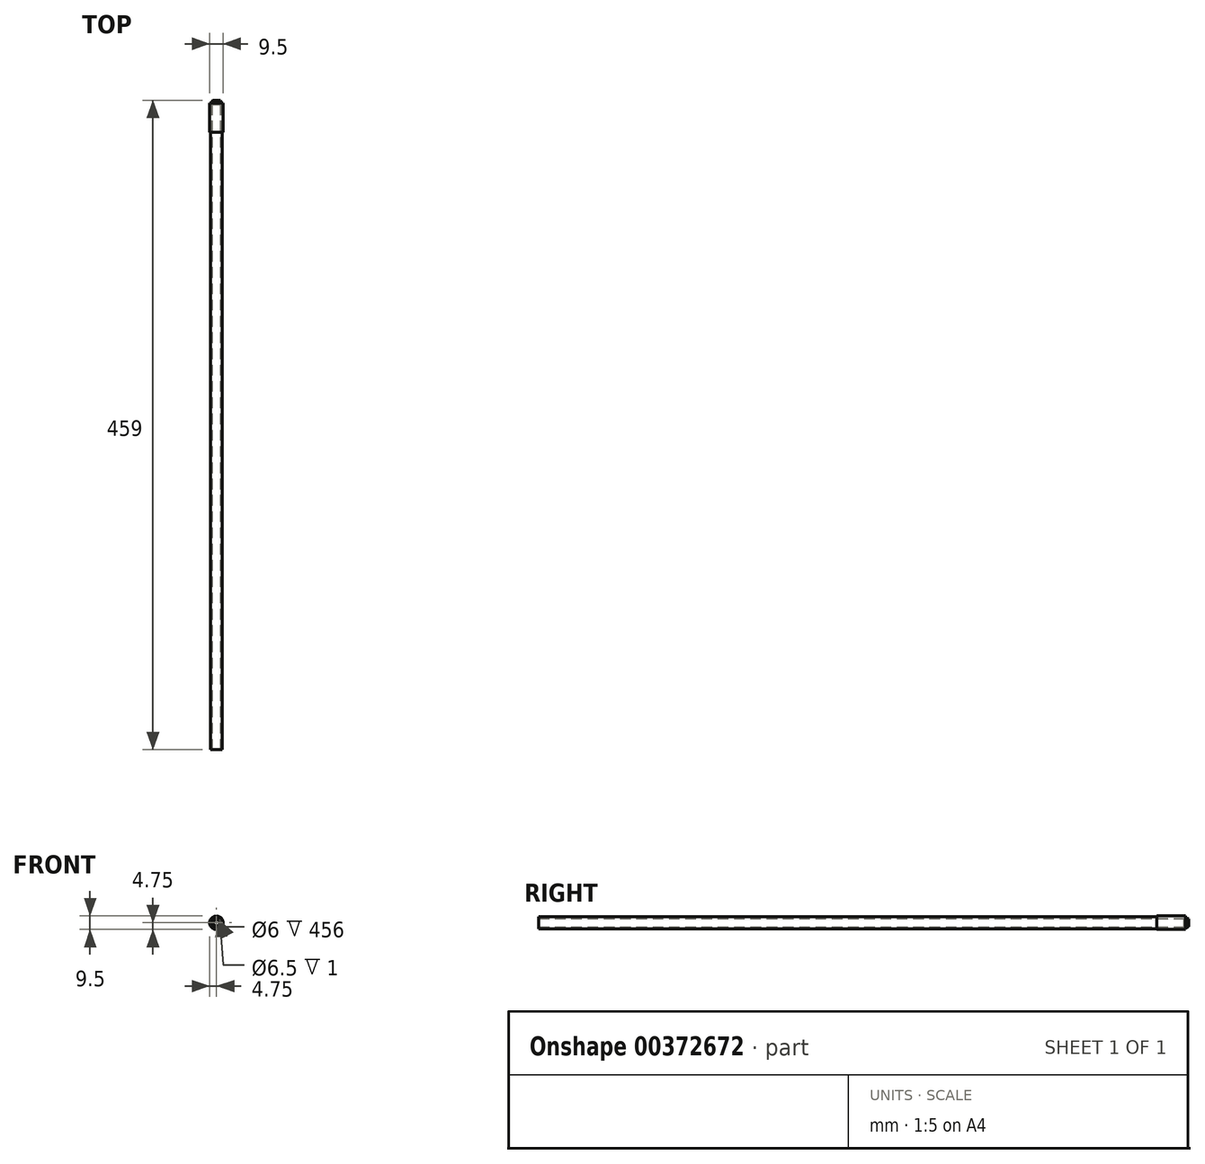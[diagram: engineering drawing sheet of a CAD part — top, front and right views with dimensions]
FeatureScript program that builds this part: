
annotation { "Feature Type Name" : "Feature", "Feature Type Description" : "" }
export const myFeature = defineFeature(function(context is Context, id is Id, definition is map)
    precondition{}
    {
        {
            var Q0;
            Q0=qCreatedBy(makeId("Front.planeOp"),FACE);
            var sketch = newSketch(context, id + "F0", { "sketchPlane" : qUnion([Q0])});
            skCircle(sketch, "E0", {"center": v(0, 0) * mm, "radius": 4.25 * mm});
            skCircle(sketch, "E1", {"center": v(0, 0) * mm, "radius": 3 * mm});
            skSolve(sketch);
        }
        {
            var Q0;
            Q0 = qSketchRegion(id + "F0", true);
            extrude(context, id + "F1", {"entities" : qUnion([Q0]), "depth" : 456 * mm});
        }
        {
            var Q0;
            Q0=qCreatedBy(makeId("Front.planeOp"),FACE);
            var sketch = newSketch(context, id + "F2", { "sketchPlane" : qUnion([Q0])});
            skCircle(sketch, "E2", {"center": v(0, 0) * mm, "radius": 4.75 * mm});
            skCircle(sketch, "E3", {"center": v(0, 0) * mm, "radius": 3.25 * mm});
            skCircle(sketch, "E4", {"center": v(0, 0) * mm, "radius": 4.25 * mm});
            skSolve(sketch);
        }
        {
            var Q0;
            Q0=makeQuery(id+"F2.imprint","IMPRINT",FACE,{"disambiguationData":[TD([[makeQuery(id+"F2.imprint","IMPRINT",EDGE,{"derivedFrom":sQuery(id+"F2.wireOp",EDGE,"E2")}),1.0]])]});
            var Q1;
            Q1=makeQuery(id+"F2.imprint","IMPRINT",FACE,{"disambiguationData":[TD([[makeQuery(id+"F2.imprint","IMPRINT",EDGE,{"derivedFrom":sQuery(id+"F2.wireOp",EDGE,"E3")}),-1.0]])]});
            extrude(context, id + "F3", {"entities" : qUnion([Q0, Q1]), "oppositeDirection" : true, "depth" : 1 * mm});
        }
        {
            var Q0;
            Q0=makeQuery(id+"F3.opExtrude","CAP_FACE",FACE,{"disambiguationData":[OSD([sQuery(id+"F2.wireOp",EDGE,"E2"),sQuery(id+"F2.wireOp",EDGE,"E4")])],"isStart":false});
            extrude(context, id + "F4", {"entities" : qUnion([Q0]), "operationType" : NewBodyOperationType.ADD, "oppositeDirection" : true, "depth" : 20.5 * mm});
        }
        {
            var Q0;
            Q0=qCreatedBy(makeId("Right.planeOp"),FACE);
            var sketch = newSketch(context, id + "F5", { "sketchPlane" : qUnion([Q0])});
            skLineSegment(sketch, "E5", {"start": v(1, 0) * mm, "end": v(5.46, 0) * mm});
            skLineSegment(sketch, "E6", {"start": v(3, 2.25) * mm, "end": v(3, 2.75) * mm});
            skLineSegment(sketch, "E7", {"start": v(3, 2.25) * mm, "end": v(1, 3.25) * mm});
            skLineSegment(sketch, "E8", {"start": v(1, 3.75) * mm, "end": v(1, 3.25) * mm});
            skLineSegment(sketch, "E9", {"start": v(1, 3.75) * mm, "end": v(3, 2.75) * mm});
            skSolve(sketch);
        }
        {
            var Q0;
            Q0=makeQuery(id+"F5.imprint","IMPRINT",FACE,{"disambiguationData":[TD([[makeQuery(id+"F5.imprint","IMPRINT",EDGE,{"derivedFrom":sQuery(id+"F5.wireOp",EDGE,"E6")}),1.0]])]});
            var Q1;
            Q1=sQuery(id+"F5.wireOp",EDGE,"E5");
            revolve(context, id + "F6", {"operationType" : NewBodyOperationType.ADD, "entities" : qUnion([Q0]), "axis" : qUnion([Q1]), "revolveType" : RevolveType.FULL});
        }
    });
